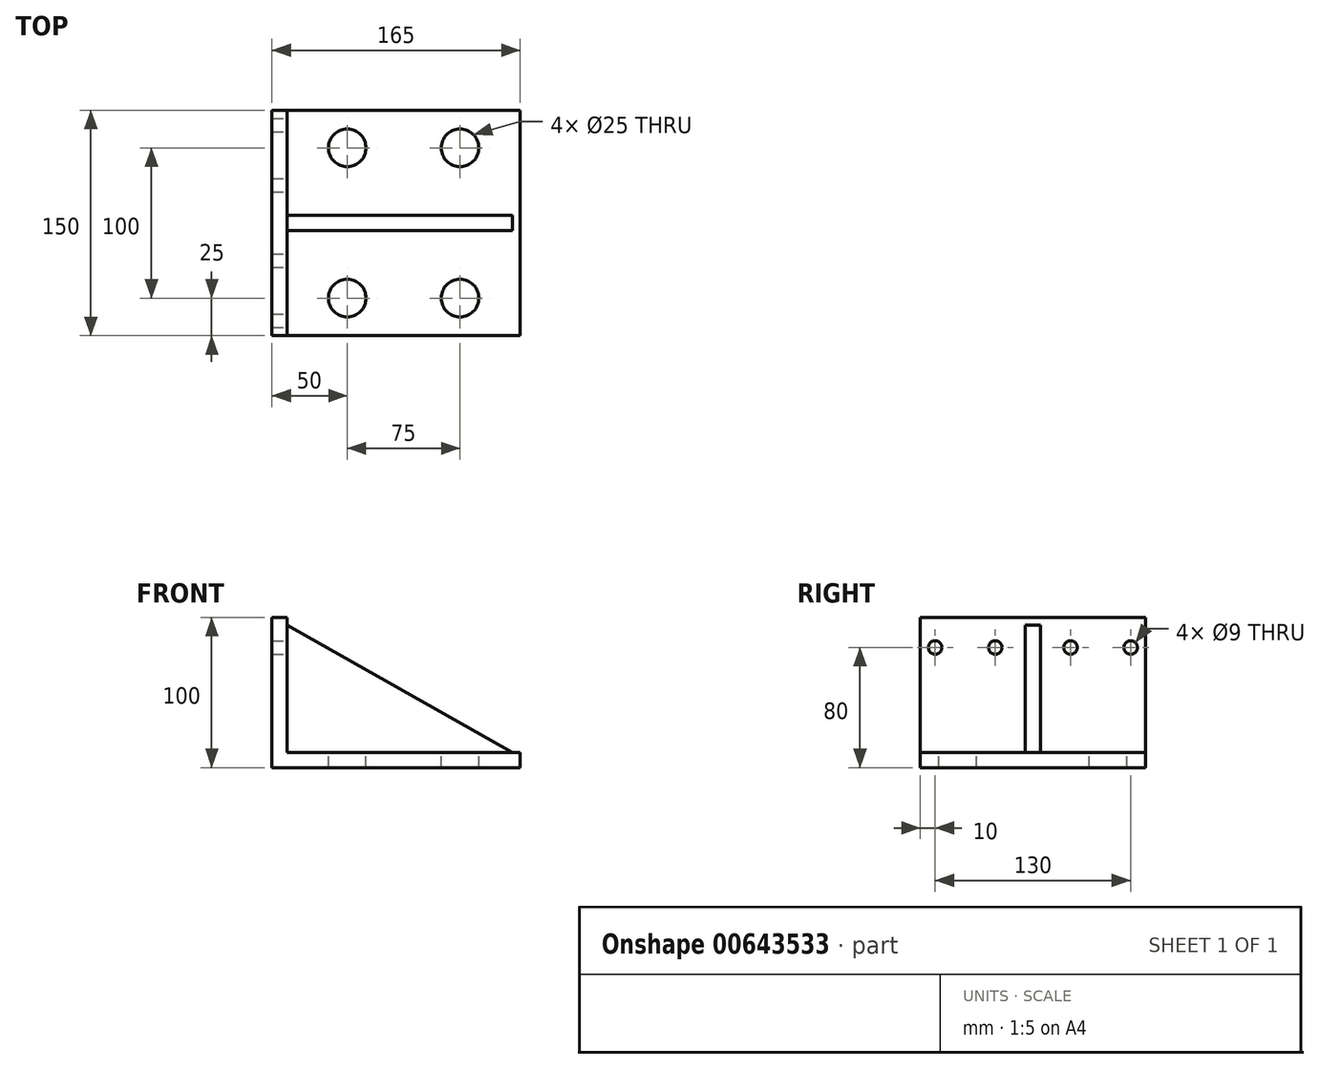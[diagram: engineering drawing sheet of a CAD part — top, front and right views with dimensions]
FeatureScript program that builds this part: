
annotation { "Feature Type Name" : "Feature", "Feature Type Description" : "" }
export const myFeature = defineFeature(function(context is Context, id is Id, definition is map)
    precondition{}
    {
        {
            var Q0;
            Q0=qCreatedBy(makeId("Front.planeOp"),FACE);
            var sketch = newSketch(context, id + "F0", { "sketchPlane" : qUnion([Q0])});
            skLineSegment(sketch, "E0", {"start": v(-10, 90) * mm, "end": v(-10, -10) * mm});
            skLineSegment(sketch, "E1", {"start": v(-10, -10) * mm, "end": v(155, -10) * mm});
            skLineSegment(sketch, "E2", {"start": v(155, -10) * mm, "end": v(155, 0) * mm});
            skLineSegment(sketch, "E3", {"start": v(155, 0) * mm, "end": v(0, 0) * mm});
            skLineSegment(sketch, "E4", {"start": v(0, 0) * mm, "end": v(0, 90) * mm});
            skLineSegment(sketch, "E5", {"start": v(0, 90) * mm, "end": v(-10, 90) * mm});
            skSolve(sketch);
        }
        {
            var Q0;
            Q0=qSketchRegion(id+"F0",true);
            extrude(context, id + "F1", {"entities" : qUnion([Q0]), "depth" : 75 * mm, "offsetDistance" : 25 * mm, "hasSecondDirection" : true, "secondDirectionOppositeDirection" : true, "secondDirectionDepth" : 75 * mm});
        }
        {
            var Q0;
            Q0=qCreatedBy(makeId("Front.planeOp"),FACE);
            var sketch = newSketch(context, id + "F2", { "sketchPlane" : qUnion([Q0])});
            skLineSegment(sketch, "E6", {"start": v(0, 85) * mm, "end": v(150, 0) * mm});
            skLineSegment(sketch, "E7", {"start": v(150, 0) * mm, "end": v(0, 0) * mm});
            skLineSegment(sketch, "E8", {"start": v(0, 0) * mm, "end": v(0, 85) * mm});
            skSolve(sketch);
        }
        {
            var Q0;
            Q0=qSketchRegion(id+"F2",true);
            extrude(context, id + "F3", {"entities" : qUnion([Q0]), "operationType" : NewBodyOperationType.ADD, "depth" : 5 * mm, "offsetDistance" : 25 * mm, "hasSecondDirection" : true, "secondDirectionOppositeDirection" : true, "secondDirectionDepth" : 5 * mm});
        }
        {
            var Q0;
            Q0=qCreatedBy(makeId("Right.planeOp"),FACE);
            var sketch = newSketch(context, id + "F4", { "sketchPlane" : qUnion([Q0])});
            skCircle(sketch, "E9", {"center": v(-65, 70) * mm, "radius": 4.5 * mm});
            skCircle(sketch, "E10", {"center": v(-25, 70) * mm, "radius": 4.5 * mm});
            skLineSegment(sketch, "E11", {"start": v(0, 90) * mm, "end": v(0, 0) * mm, "construction": true});
            skLineSegment(sketch, "E12", {"start": v(-65, 70) * mm, "end": v(0, 70) * mm, "construction": true});
            skCircle(sketch, "E13.MirrorC", {"center": v(25, 70) * mm, "radius": 4.5 * mm});
            skCircle(sketch, "E14.MirrorC", {"center": v(65, 70) * mm, "radius": 4.5 * mm});
            skLineSegment(sketch, "E15.MirrorCS", {"start": v(65, 70) * mm, "end": v(0, 70) * mm, "construction": true});
            skSolve(sketch);
        }
        {
            var Q0;
            Q0=qSketchRegion(id+"F4",true);
            extrude(context, id + "F5", {"entities" : qUnion([Q0]), "operationType" : NewBodyOperationType.REMOVE, "endBound" : BoundingType.UP_TO_NEXT, "oppositeDirection" : true, "depth" : 25 * mm, "offsetDistance" : 25 * mm});
        }
        {
            var Q0;
            Q0=qCreatedBy(makeId("Top.planeOp"),FACE);
            var sketch = newSketch(context, id + "F6", { "sketchPlane" : qUnion([Q0])});
            skCircle(sketch, "E16", {"center": v(40, 50) * mm, "radius": 12.5 * mm});
            skCircle(sketch, "E17", {"center": v(115, 50) * mm, "radius": 12.5 * mm});
            skLineSegment(sketch, "E18", {"start": v(0, 0) * mm, "end": v(155, 0) * mm, "construction": true});
            skCircle(sketch, "E19.MirrorC", {"center": v(115, -50) * mm, "radius": 12.5 * mm});
            skCircle(sketch, "E20.MirrorC", {"center": v(40, -50) * mm, "radius": 12.5 * mm});
            skSolve(sketch);
        }
        {
            var Q0;
            Q0=qSketchRegion(id+"F6",true);
            extrude(context, id + "F7", {"entities" : qUnion([Q0]), "operationType" : NewBodyOperationType.REMOVE, "endBound" : BoundingType.UP_TO_NEXT, "oppositeDirection" : true, "depth" : 25 * mm, "offsetDistance" : 25 * mm});
        }
    });
